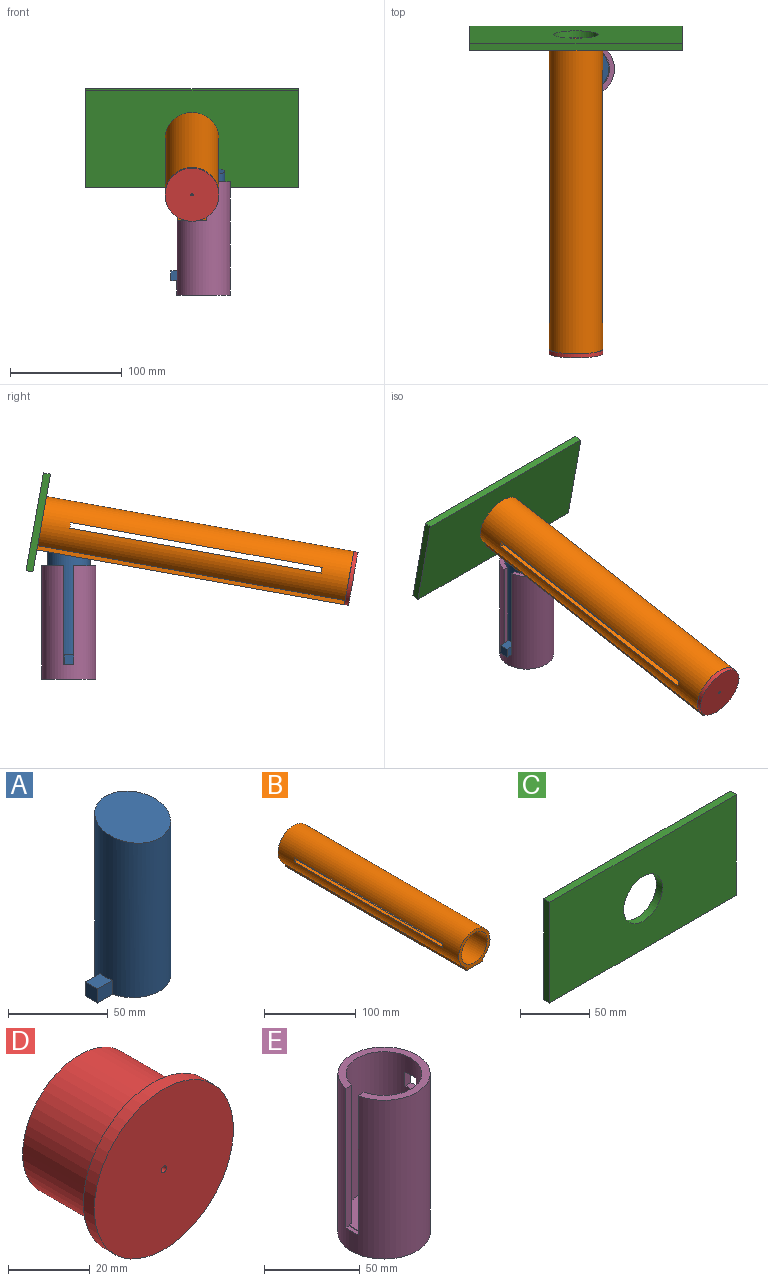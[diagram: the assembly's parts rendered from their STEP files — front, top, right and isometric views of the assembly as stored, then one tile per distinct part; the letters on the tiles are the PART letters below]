
ASSEMBLY  parts=5 mates=4
PART A: 7 faces, bbox 48.3x38.1x101 mm
  f0: cylinder r=19.05mm len=100.98mm, axis (0,0,-1), area 11602.6mm2, adj f1,f2,f3,f4,f6
  f1: plane 48.26x38.1mm, normal (0,0,-1), area 1229.3mm2, adj f0,f2,f3,f5
  f2: plane 10.66x8.64mm, normal (0,1,0), area 92mm2, adj f0,f1,f4,f5
  f3: plane 10.66x8.64mm, normal (0,-1,0), area 92mm2, adj f0,f1,f4,f5
  f4: plane 10.66x8.64mm, normal (0,0,1), area 89.2mm2, adj f0,f2,f3,f5
  f5: plane 8.64x8.64mm, normal (-1,0,0), area 74.6mm2, adj f1,f2,f3,f4
  f6: plane 38.1x38.1mm, normal (0,-0.18,0.98), area 1158.2mm2, adj f0
PART B: 15 faces, bbox 48.3x279.4x48.5 mm
  f0: cylinder r=24.13mm len=279.4mm, axis (0,1,0), area 32547.1mm2, adj f2,f3,f4,f6,f7,f8,f9,f10
  f1: cylinder r=19.81mm len=279.4mm, axis (0,1,0), area 32431.6mm2, adj f2,f3,f7,f8,f9,f10,f11,f12
  f2: plane 48.46x48.26mm, normal (0,-1,0), area 630.7mm2, adj f0,f1,f4,f5,f6
  f3: plane 48.46x48.26mm, normal (0,1,0), area 630.7mm2, adj f0,f1,f4,f5,f6
  f4: plane 279.4x3.81mm, normal (-1,0,0), area 1064.5mm2, adj f0,f2,f3,f5
  f5: plane 279.4x25.4mm, normal (0,0,-1), area 7096.8mm2, adj f2,f3,f4,f6
  f6: plane 279.4x3.81mm, normal (1,0,0), area 1064.5mm2, adj f0,f2,f3,f5
  f7: plane 228.6x4.32mm, normal (0,0,1), area 987.1mm2, adj f0,f1,f8,f10
  f8: plane 5.08x4.98mm, normal (0,1,0), area 22.1mm2, adj f0,f1,f7,f9
  f9: plane 228.6x4.44mm, normal (0,0,-1), area 1014.9mm2, adj f0,f1,f8,f10
  f10: plane 5.08x4.98mm, normal (0,-1,0), area 22.1mm2, adj f0,f1,f7,f9
  f11: plane 5.08x4.98mm, normal (0,-1,0), area 22.1mm2, adj f0,f1,f12,f14
  f12: plane 228.6x4.44mm, normal (0,0,-1), area 1014.9mm2, adj f0,f1,f11,f13
  f13: plane 5.08x4.98mm, normal (0,1,0), area 22.1mm2, adj f0,f1,f12,f14
  f14: plane 228.6x4.32mm, normal (0,0,1), area 987.1mm2, adj f0,f1,f11,f13
PART C: 7 faces, bbox 190.5x6.4x88.9 mm
  f0: plane 88.9x6.35mm, normal (-1,0,0), area 564.5mm2, adj f1,f3,f4,f5
  f1: plane 190.5x6.35mm, normal (0,0,-1), area 1209.7mm2, adj f0,f2,f4,f5
  f2: plane 88.9x6.35mm, normal (1,0,0), area 564.5mm2, adj f1,f3,f4,f5
  f3: plane 190.5x6.35mm, normal (0,0,1), area 1209.7mm2, adj f0,f2,f4,f5
  f4: plane 190.5x88.9mm, normal (0,-1,0), area 15702.3mm2, adj f0,f1,f2,f3,f6
  f5: plane 190.5x88.9mm, normal (0,1,0), area 15702.3mm2, adj f0,f1,f2,f3,f6
  f6: cylinder r=19.81mm len=39.62mm, axis (0,-1,0), area 790.5mm2, adj f4,f5
PART D: 8 faces, bbox 48.3x29.2x48.3 mm
  f0: cylinder r=17.78mm len=35.56mm, axis (0,1,0), area 2837.6mm2, adj f2,f6
  f1: cylinder r=19.81mm len=39.62mm, axis (0,1,0), area 3161.9mm2, adj f2,f3
  f2: plane 39.62x39.62mm, normal (0,1,0), area 240mm2, adj f0,f1
  f3: plane 48.26x48.26mm, normal (0,1,0), area 596.1mm2, adj f1,f5
  f4: plane 48.26x48.26mm, normal (0,-1,0), area 1826.4mm2, adj f5,f7
  f5: cylinder r=24.13mm len=48.26mm, axis (0,1,0), area 577.6mm2, adj f3,f4
  f6: plane 35.56x35.56mm, normal (0,1,0), area 990.3mm2, adj f0,f7
  f7: cylinder r=0.95mm len=3.81mm, axis (0,-1,0), area 22.8mm2, adj f4,f6
PART E: 25 faces, bbox 48.3x48.3x101.6 mm
  f0: cylinder r=19.81mm len=88.39mm, axis (0,0,-1), area 9905.8mm2, adj f1,f4,f5,f7,f8,f9,f10,f11
  f1: plane 48.26x47.84mm, normal (0,0,1), area 557mm2, adj f0,f2,f4,f5
  f2: cylinder r=24.13mm len=101.6mm, axis (0,0,-1), area 14304.9mm2, adj f1,f3,f4,f5,f6,f7,f8,f9
  f3: plane 48.26x48.26mm, normal (0,0,-1), area 1829.2mm2, adj f2
  f4: plane 88.9x4.41mm, normal (0,1,0), area 391.3mm2, adj f0,f1,f2,f6,f23,f24
  f5: plane 88.9x4.41mm, normal (0,-1,0), area 391.3mm2, adj f0,f1,f2,f6,f23,f24
  f6: plane 8.99x3mm, normal (0,0,1), area 22.8mm2, adj f2,f4,f5,f23
  f7: plane 8.89x4.39mm, normal (0,-1,0), area 39mm2, adj f0,f2,f8,f10
  f8: plane 8.26x4.79mm, normal (0,0,-1), area 35.9mm2, adj f0,f2,f7,f9
  f9: plane 8.89x4.4mm, normal (0,1,0), area 39.2mm2, adj f0,f2,f8,f10
  f10: plane 8.26x4.79mm, normal (0,0,1), area 35.9mm2, adj f0,f2,f7,f9
  f11: plane 8.89x4.39mm, normal (0,-1,0), area 39mm2, adj f0,f2,f12,f14
  f12: plane 8.26x4.79mm, normal (0,0,-1), area 35.9mm2, adj f0,f2,f11,f13
  f13: plane 8.89x4.4mm, normal (0,1,0), area 39.2mm2, adj f0,f2,f12,f14
  f14: plane 8.26x4.79mm, normal (0,0,1), area 35.9mm2, adj f0,f2,f11,f13
  f15: plane 8.89x4.39mm, normal (0,-1,0), area 39mm2, adj f0,f2,f16,f18
  f16: plane 8.26x4.79mm, normal (0,0,-1), area 35.9mm2, adj f0,f2,f15,f17
  f17: plane 8.89x4.4mm, normal (0,1,0), area 39.2mm2, adj f0,f2,f16,f18
  f18: plane 8.26x4.79mm, normal (0,0,1), area 35.9mm2, adj f0,f2,f15,f17
  f19: plane 8.89x4.39mm, normal (0,-1,0), area 39mm2, adj f0,f2,f20,f22
  f20: plane 8.26x4.79mm, normal (0,0,-1), area 35.9mm2, adj f0,f2,f19,f21
  f21: plane 8.89x4.4mm, normal (0,1,0), area 39.2mm2, adj f0,f2,f20,f22
  f22: plane 8.26x4.79mm, normal (0,0,1), area 35.9mm2, adj f0,f2,f19,f21
  f23: cylinder r=21.61mm len=8.99mm, axis (0,0,-1), area 4.6mm2, adj f4,f5,f6,f24
  f24: plane 41.42x39.62mm, normal (0,0,1), area 1249.4mm2, adj f0,f4,f5,f23
PLACE A t=(86.16,126.24,-76.53)mm
PLACE B rot(axis=(1,0,0),10.1deg) t=(75.87,150.53,50.09)mm
PLACE C rot(axis=(1,0,0),10.1deg) t=(-19.38,164.6,7.45)mm
PLACE D rot(axis=(1,0,0),10.1deg) t=(75.87,-99.51,5.4)mm
PLACE E t=(86.16,126.24,-89.5)mm fixed
MATE slider E.f0 <-> A.f0  axis (0,0,-1) through (86.16,126.24,-32.09)mm
MATE fastened B.f1 <-> D.f5  axis (0,-0.98,-0.18) through (75.87,-124.51,0.93)mm
MATE planar A.f6 <-> B.f5  axis (0,-0.18,0.98) through (86.16,126.24,21.03)mm
MATE fastened C.f6 <-> B.f1  axis (0,-0.98,-0.18) through (75.87,150.53,50.09)mm
